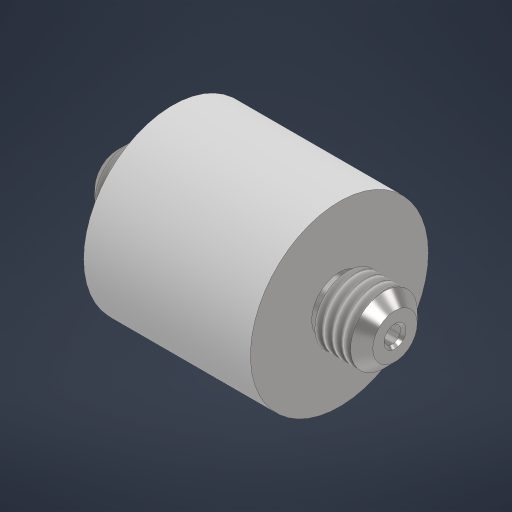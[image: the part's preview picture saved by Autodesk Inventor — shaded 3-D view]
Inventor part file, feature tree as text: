
AUTODESK INVENTOR PART (.ipt)
format: ipt  version: 2024.3 (Build 283343000, 343)  size: 262,656 bytes
history: native  units: mm
features: other x4, direct_edit x1, extrude x1, sketch x1, projected_geometry x1
ambient origin geometry x8: Origin, YZ Plane, XZ Plane, XY Plane, X Axis, Y Axis, Z Axis, Center Point
bodies: Solid1 (feature_tree)
feature tree (8):
  other  "HM1-1002.ipt"
  direct_edit  "Direct Edit1"
  extrude  "Extrusion1"  Depth=10.0mm
  other  "Solid1::HM1-1002.ipt"
  other  "TaggingFeature1"
  sketch  "Sketch1"  dims[d0=10.0mm d2=1.0mm d3=32.0mm d4=10.0mm d5=0.0mm d6=0.5mm d7=0.872665mm]
  projected_geometry  "Projected Loop1"
  other  "Delete1"
